# Revit family: OASIS SH4P-6032_C STD
name_source: partatom
category: Plumbing Fixtures
units: mm (PartAtom-declared; Revit-internal decimal feet)

## family parameters
Always vertical = Yes
Cut with Voids When Loaded = No
OmniClass Number = 23.45.00.00
OmniClass Title = Sanitary, Laundry, and Cleaning Equipment
Part Type = Normal
Room Calculation Point = No
Round Connector Dimension = Use Diameter
Shared = No
Work Plane-Based = No

## types (3) — shared parameters
BIM Model By = www.shive-hattery.com
Color = <By Category>
Default Elevation = 0"
Grab Bar Finish = <By Category>
Manufacturer = OASIS
Type Comments = Shower
URL = www.oasisbath.com

## per-type parameters (varying)
| type | Bar_Horz_Back | Bar_Horz_Side | Bar_Vert | Model |
| Base model & FH packages | No | No | No | SH4P-6032 STD/(Base Model,FH) |
| BP1-60 package | Yes | Yes | No | SH4P-6032 STD/BP1-60 |
| BP2-60 package | Yes | Yes | Yes | SH4P-6032 STD/BP2-60 |

## geometry (parser evidence)
native form markers: Blend x4, Sweep x17
no freeform markers — native parametric forms only
